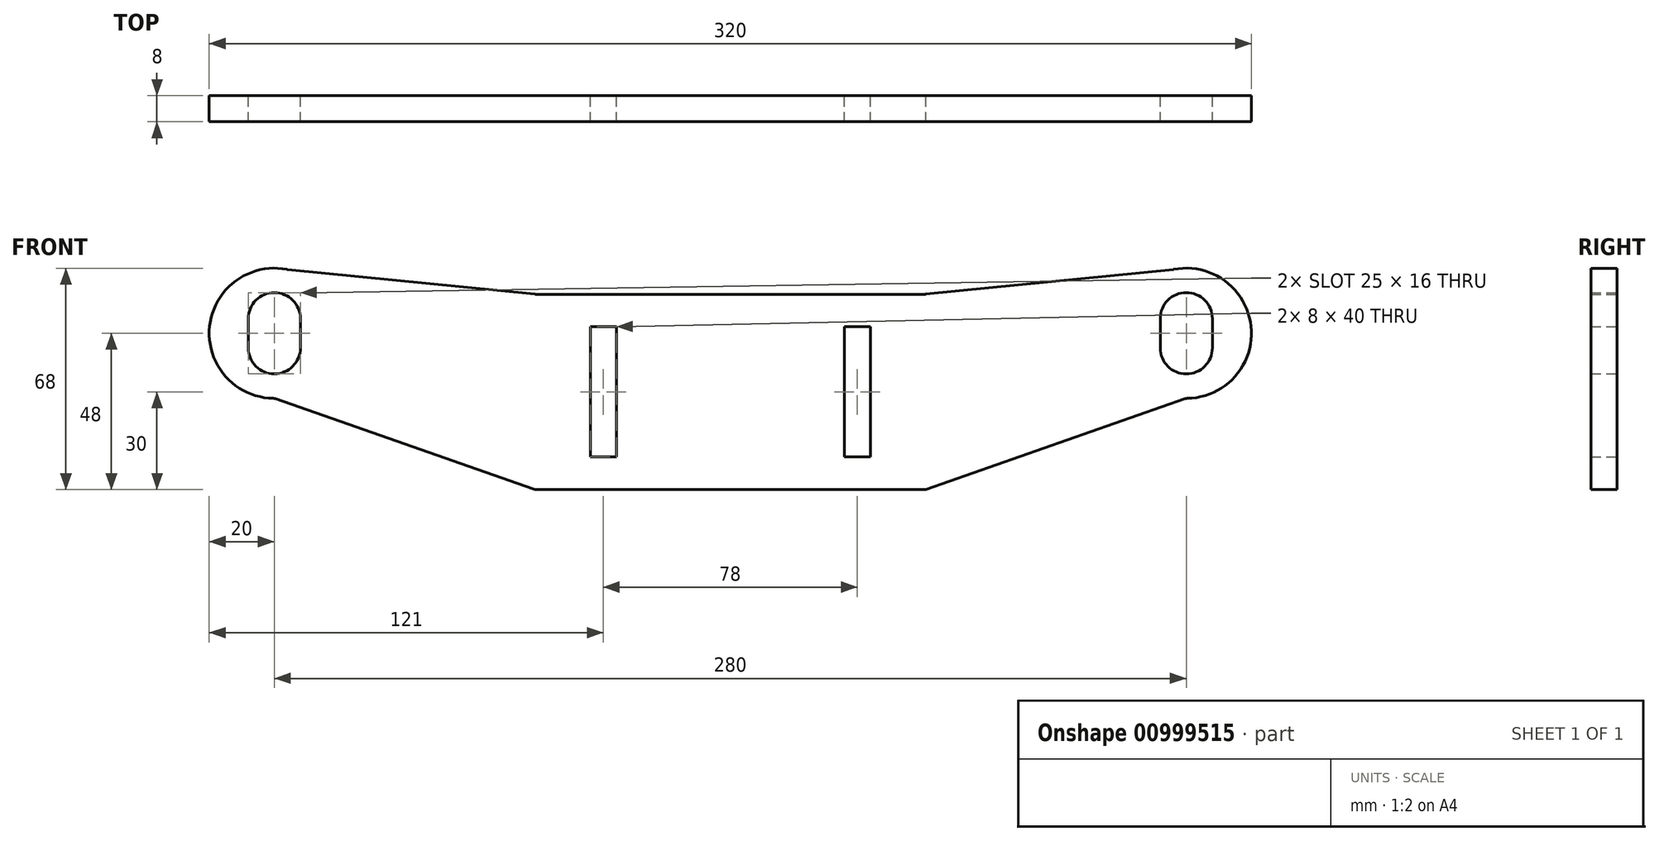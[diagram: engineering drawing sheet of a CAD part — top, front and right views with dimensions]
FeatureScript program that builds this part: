
annotation { "Feature Type Name" : "Feature", "Feature Type Description" : "" }
export const myFeature = defineFeature(function(context is Context, id is Id, definition is map)
    precondition{}
    {
        {
            var Q0;
            Q0=qCreatedBy(makeId("Front.planeOp"),FACE);
            var sketch = newSketch(context, id + "F0", { "sketchPlane" : qUnion([Q0])});
            skLineSegment(sketch, "E0.bottom", {"start": v(0, 0) * mm, "end": v(-120, 0) * mm});
            skLineSegment(sketch, "E0.top", {"start": v(0, -60) * mm, "end": v(-120, -60) * mm});
            skLineSegment(sketch, "E0.left", {"start": v(0, 0) * mm, "end": v(0, -60) * mm});
            skLineSegment(sketch, "E0.right", {"start": v(-120, 0) * mm, "end": v(-120, -60) * mm});
            skLineSegment(sketch, "E1", {"start": v(0, 0) * mm, "end": v(80, 8) * mm});
            skLineSegment(sketch, "E2", {"start": v(80, 8) * mm, "end": v(80, -32) * mm});
            skLineSegment(sketch, "E3", {"start": v(80, -32) * mm, "end": v(0, -60) * mm});
            skLineSegment(sketch, "E4", {"start": v(-120, 0) * mm, "end": v(-200, 8) * mm});
            skLineSegment(sketch, "E5", {"start": v(-200, 8) * mm, "end": v(-200, -32) * mm});
            skLineSegment(sketch, "E6", {"start": v(-200, -32) * mm, "end": v(-120, -60) * mm});
            skPoint(sketch, "E7.centerSnap0", {"position": v(-200, -12) * mm});
            skCircle(sketch, "E8", {"center": v(80, -12) * mm, "radius": 20 * mm});
            skCircle(sketch, "E9", {"center": v(-200, -12) * mm, "radius": 20 * mm});
            skLineSegment(sketch, "E10.bottom", {"start": v(-103, -10) * mm, "end": v(-95, -10) * mm});
            skLineSegment(sketch, "E10.top", {"start": v(-103, -50) * mm, "end": v(-95, -50) * mm});
            skLineSegment(sketch, "E10.left", {"start": v(-103, -10) * mm, "end": v(-103, -50) * mm});
            skLineSegment(sketch, "E10.right", {"start": v(-95, -10) * mm, "end": v(-95, -50) * mm});
            skLineSegment(sketch, "E11.bottom", {"start": v(-25, -10) * mm, "end": v(-17, -10) * mm});
            skLineSegment(sketch, "E11.top", {"start": v(-25, -50) * mm, "end": v(-17, -50) * mm});
            skLineSegment(sketch, "E11.left", {"start": v(-25, -10) * mm, "end": v(-25, -50) * mm});
            skLineSegment(sketch, "E11.right", {"start": v(-17, -10) * mm, "end": v(-17, -50) * mm});
            skLineSegment(sketch, "E12.bottom", {"start": v(-208, -7.5) * mm, "end": v(-192, -7.5) * mm});
            skLineSegment(sketch, "E12.top", {"start": v(-208, -16.5) * mm, "end": v(-192, -16.5) * mm});
            skLineSegment(sketch, "E12.left", {"start": v(-208, -7.5) * mm, "end": v(-208, -16.5) * mm});
            skLineSegment(sketch, "E12.right", {"start": v(-192, -7.5) * mm, "end": v(-192, -16.5) * mm});
            skCircle(sketch, "E13", {"center": v(-200, -7.5) * mm, "radius": 8 * mm});
            skCircle(sketch, "E14", {"center": v(-200, -16.5) * mm, "radius": 8 * mm});
            skLineSegment(sketch, "E15.bottom", {"start": v(72, -7.5) * mm, "end": v(88, -7.5) * mm});
            skLineSegment(sketch, "E15.top", {"start": v(72, -16.5) * mm, "end": v(88, -16.5) * mm});
            skLineSegment(sketch, "E15.left", {"start": v(72, -7.5) * mm, "end": v(72, -16.5) * mm});
            skLineSegment(sketch, "E15.right", {"start": v(88, -7.5) * mm, "end": v(88, -16.5) * mm});
            skCircle(sketch, "E16", {"center": v(80, -7.5) * mm, "radius": 8 * mm});
            skCircle(sketch, "E17", {"center": v(80, -16.5) * mm, "radius": 8 * mm});
            skSolve(sketch);
        }
        {
            var Q0;
            Q0 = qSketchRegion(id + "F0", true);
            extrude(context, id + "F1", {"entities" : qUnion([Q0]), "depth" : 8 * mm, "offsetDistance" : 25 * mm});
        }
        {
            var Q0;
            Q0=makeQuery(id+"F1.opExtrude","SWEPT_EDGE",EDGE,{"disambiguationData":[OSD([sQuery(id+"F0.wireOp",EDGE,"E0.bottom"),sQuery(id+"F0.wireOp",EDGE,"E0.right"),sQuery(id+"F0.wireOp",EDGE,"E4")])]});
            var Q1;
            Q1=makeQuery(id+"F1.opExtrude","SWEPT_EDGE",EDGE,{"disambiguationData":[OSD([sQuery(id+"F0.wireOp",EDGE,"E0.bottom"),sQuery(id+"F0.wireOp",EDGE,"E0.left"),sQuery(id+"F0.wireOp",EDGE,"E1")])]});
            var Q2;
            Q2=makeQuery(id+"F1.opExtrude","SWEPT_EDGE",EDGE,{"disambiguationData":[OSD([sQuery(id+"F0.wireOp",EDGE,"E0.top"),sQuery(id+"F0.wireOp",EDGE,"E0.right"),sQuery(id+"F0.wireOp",EDGE,"E6")])]});
            var Q3;
            Q3=makeQuery(id+"F1.opExtrude","SWEPT_EDGE",EDGE,{"disambiguationData":[OSD([sQuery(id+"F0.wireOp",EDGE,"E5"),sQuery(id+"F0.wireOp",EDGE,"E6"),sQuery(id+"F0.wireOp",EDGE,"E9")])]});
            var Q4;
            Q4=makeQuery(id+"F1.opExtrude","SWEPT_EDGE",EDGE,{"disambiguationData":[OSD([sQuery(id+"F0.wireOp",EDGE,"E2"),sQuery(id+"F0.wireOp",EDGE,"E3"),sQuery(id+"F0.wireOp",EDGE,"E8")])]});
            var Q5;
            Q5=makeQuery(id+"F1.opExtrude","SWEPT_EDGE",EDGE,{"disambiguationData":[OSD([sQuery(id+"F0.wireOp",EDGE,"E1"),sQuery(id+"F0.wireOp",EDGE,"E2"),sQuery(id+"F0.wireOp",EDGE,"E8")])]});
            var Q6;
            Q6=makeQuery(id+"F1.opExtrude","SWEPT_EDGE",EDGE,{"disambiguationData":[OSD([sQuery(id+"F0.wireOp",EDGE,"E4"),sQuery(id+"F0.wireOp",EDGE,"E5"),sQuery(id+"F0.wireOp",EDGE,"E9")])]});
            fillet(context, id + "F2", {"entities" : qUnion([Q0, Q1, Q2, Q3, Q4, Q5, Q6]), "radius" : 2 * mm, "tangentPropagation" : true, "allowEdgeOverflow" : false});
        }
    });
